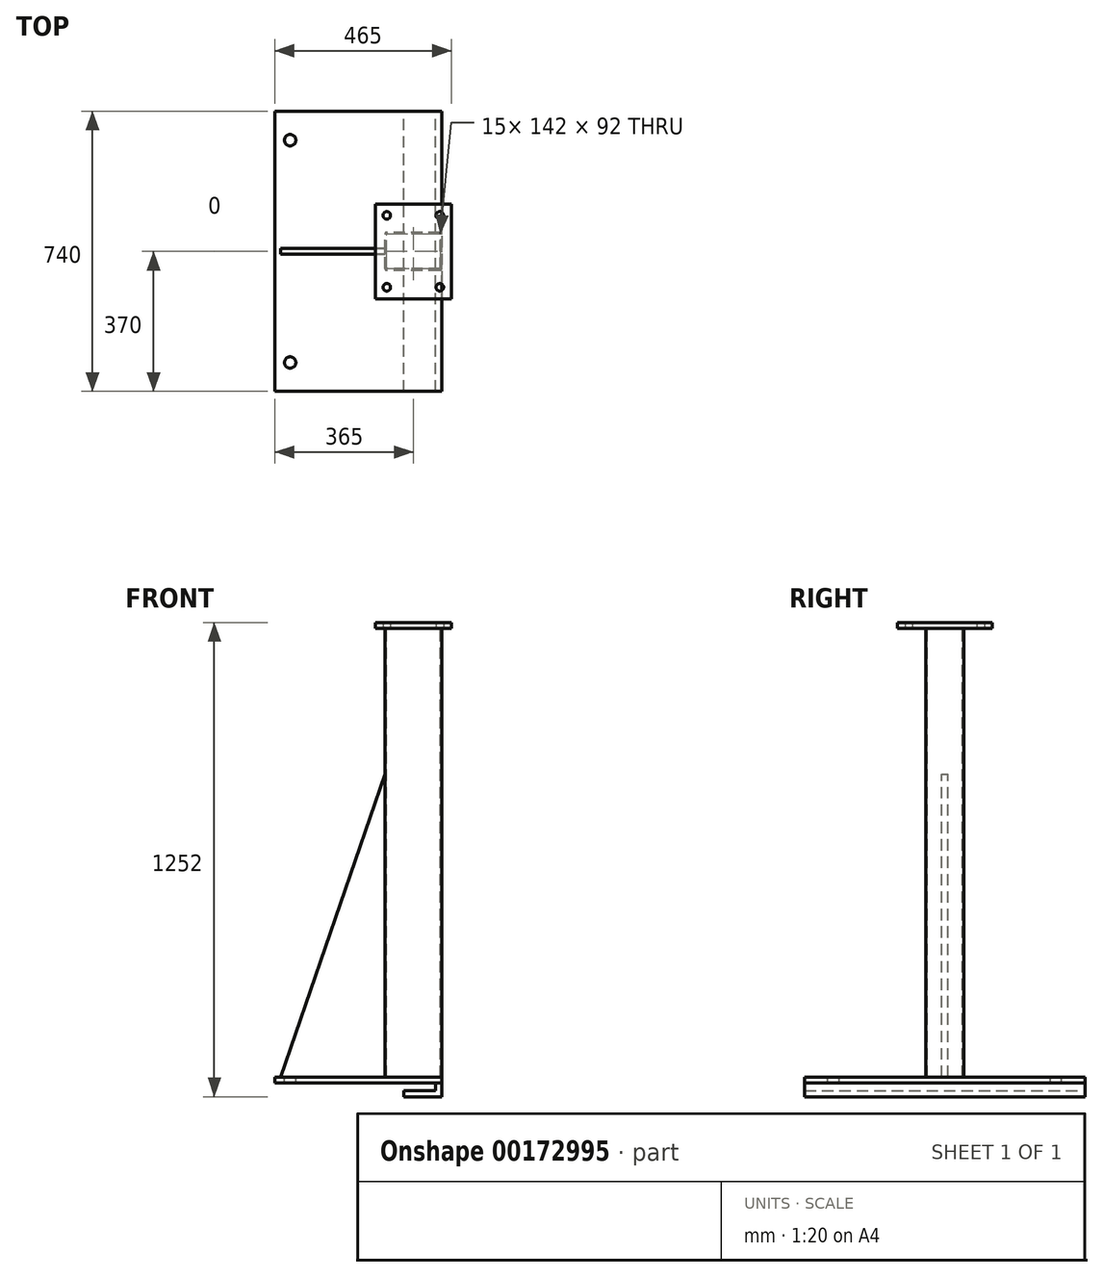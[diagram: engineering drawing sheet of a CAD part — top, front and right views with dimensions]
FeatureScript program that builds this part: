
annotation { "Feature Type Name" : "Feature", "Feature Type Description" : "" }
export const myFeature = defineFeature(function(context is Context, id is Id, definition is map)
    precondition{}
    {
        {
            var Q0;
            Q0=qCreatedBy(makeId("Top.planeOp"),FACE);
            var sketch = newSketch(context, id + "F0", { "sketchPlane" : qUnion([Q0])});
            skLineSegment(sketch, "E0.bottom", {"start": v(0, 0) * mm, "end": v(-150, 0) * mm});
            skLineSegment(sketch, "E0.top", {"start": v(0, 100) * mm, "end": v(-150, 100) * mm});
            skLineSegment(sketch, "E0.left", {"start": v(0, 0) * mm, "end": v(0, 100) * mm});
            skLineSegment(sketch, "E0.right", {"start": v(-150, 0) * mm, "end": v(-150, 100) * mm});
            skLineSegment(sketch, "E1.0", {"start": v(-4, 96) * mm, "end": v(-146, 96) * mm});
            skLineSegment(sketch, "E1.1", {"start": v(-4, 4) * mm, "end": v(-4, 96) * mm});
            skLineSegment(sketch, "E1.2", {"start": v(-4, 4) * mm, "end": v(-146, 4) * mm});
            skLineSegment(sketch, "E1.3", {"start": v(-146, 4) * mm, "end": v(-146, 96) * mm});
            skSolve(sketch);
        }
        {
            var Q0;
            Q0=makeQuery(id+"F0.imprint","IMPRINT",FACE,{"disambiguationData":[TD([[makeQuery(id+"F0.imprint","IMPRINT",EDGE,{"derivedFrom":sQuery(id+"F0.wireOp",EDGE,"E0.bottom")}),-1.0]])]});
            extrude(context, id + "F1", {"entities" : qUnion([Q0]), "oppositeDirection" : true, "depth" : 1184 * mm});
        }
        {
            var Q0;
            Q0=makeQuery(id+"F1.opExtrude","CAP_FACE",FACE,{"disambiguationData":[OSD([sQuery(id+"F0.wireOp",EDGE,"E0.bottom"),sQuery(id+"F0.wireOp",EDGE,"E0.top"),sQuery(id+"F0.wireOp",EDGE,"E0.left"),sQuery(id+"F0.wireOp",EDGE,"E0.right"),sQuery(id+"F0.wireOp",EDGE,"E1.0"),sQuery(id+"F0.wireOp",EDGE,"E1.1"),sQuery(id+"F0.wireOp",EDGE,"E1.2"),sQuery(id+"F0.wireOp",EDGE,"E1.3")])],"isStart":false});
            var sketch = newSketch(context, id + "F2", { "sketchPlane" : qUnion([Q0])});
            skLineSegment(sketch, "E2", {"start": v(0, 0) * mm, "end": v(0, 320) * mm});
            skLineSegment(sketch, "E3", {"start": v(0, -100) * mm, "end": v(0, -420) * mm});
            skLineSegment(sketch, "E4", {"start": v(0, 320) * mm, "end": v(-440, 320) * mm});
            skLineSegment(sketch, "E5", {"start": v(-440, 320) * mm, "end": v(-440, -420) * mm});
            skLineSegment(sketch, "E6", {"start": v(-440, -420) * mm, "end": v(0, -420) * mm});
            skCircle(sketch, "E7", {"center": v(-400, 243.5) * mm, "radius": 15 * mm});
            skLineSegment(sketch, "E8", {"start": v(-440, -50) * mm, "end": v(0, -50) * mm, "construction": true});
            skCircle(sketch, "E9.MirrorC", {"center": v(-400, -343.5) * mm, "radius": 15 * mm});
            skLineSegment(sketch, "E10", {"start": v(0, 0) * mm, "end": v(0, -100) * mm});
            skSolve(sketch);
        }
        {
            var Q0;
            Q0=makeQuery(id+"F2.imprint","IMPRINT",FACE,{"disambiguationData":[TD([[makeQuery(id+"F2.imprint","IMPRINT",EDGE,{"derivedFrom":sQuery(id+"F2.wireOp",EDGE,"E2")}),1.0]])]});
            var Q1;
            Q1=makeQuery(id+"F2.imprint","IMPRINT",FACE,{"disambiguationData":[TD([[makeQuery(id+"F2.imprint","IMPRINT",EDGE,{"derivedFrom":sQuery(id+"F2.wireOp",EDGE,"E10")}),-1.0]])]});
            var Q2;
            Q2=makeQuery(id+"F2.imprint","IMPRINT",FACE,{"disambiguationData":[TD([[makeQuery(id+"F2.imprint","IMPRINT",EDGE,{"derivedFrom":makeQuery(id+"F1.opExtrude","CAP_EDGE",EDGE,{"disambiguationData":[OSD([sQuery(id+"F0.wireOp",EDGE,"E1.0")])],"isStart":false})}),-1.0]])]});
            extrude(context, id + "F3", {"entities" : qUnion([Q0, Q1, Q2]), "depth" : 16 * mm});
        }
        {
            var Q0;
            Q0=makeQuery(id+"F1.opExtrude","SWEPT_FACE",FACE,{"disambiguationData":[OSD([sQuery(id+"F0.wireOp",EDGE,"E0.bottom")])]});
            cPlane(context, id + "F4", {"entities" : qUnion([Q0]), "cplaneType" : CPlaneType.OFFSET, "offset" : 50 * mm, "oppositeDirection" : true, "width" : 150 * mm, "height" : 150 * mm});
        }
        {
            var Q0;
            Q0=qCreatedBy(id+"F4.planeOp",FACE);
            var sketch = newSketch(context, id + "F5", { "sketchPlane" : qUnion([Q0])});
            skLineSegment(sketch, "E11.0", {"start": v(0, -1184) * mm, "end": v(-440, -1184) * mm});
            skLineSegment(sketch, "E11.1", {"start": v(-150, -1184) * mm, "end": v(-150, 0) * mm});
            skLineSegment(sketch, "E12", {"start": v(-425, -1184) * mm, "end": v(-150, -384) * mm});
            skSolve(sketch);
        }
        {
            var Q0;
            Q0 = qSketchRegion(id + "F5", true);
            extrude(context, id + "F6", {"entities" : qUnion([Q0]), "endBound" : BoundingType.SYMMETRIC, "depth" : 16 * mm});
        }
        {
            var Q0;
            Q0=qCreatedBy(id+"F4.planeOp",FACE);
            var sketch = newSketch(context, id + "F7", { "sketchPlane" : qUnion([Q0])});
            skLineSegment(sketch, "E13.0", {"start": v(0, -1200) * mm, "end": v(-440, -1200) * mm});
            skLineSegment(sketch, "E13.1", {"start": v(0, -1200) * mm, "end": v(0, -1184) * mm});
            skLineSegment(sketch, "E14", {"start": v(0, -1200) * mm, "end": v(0, -1236) * mm});
            skLineSegment(sketch, "E15", {"start": v(0, -1236) * mm, "end": v(-100, -1236) * mm});
            skLineSegment(sketch, "E16", {"start": v(-100, -1236) * mm, "end": v(-100, -1220) * mm});
            skLineSegment(sketch, "E17", {"start": v(-100, -1220) * mm, "end": v(-16, -1220) * mm});
            skLineSegment(sketch, "E18", {"start": v(-16, -1220) * mm, "end": v(-16, -1200) * mm});
            skSolve(sketch);
        }
        {
            var Q0;
            {var subQ0=sQuery(id+"F7.wireOp",EDGE,"E14");Q0=makeQuery(id+"F7.imprint","IMPRINT",FACE,{"disambiguationData":[TD([[makeQuery(id+"F7.imprint","IMPRINT",EDGE,{"derivedFrom":subQ0}),-1.0]])]});}
            extrude(context, id + "F8", {"entities" : qUnion([Q0]), "endBound" : BoundingType.SYMMETRIC, "depth" : 740 * mm});
        }
        {
            var Q0;
            Q0=makeQuery(id+"F1.opExtrude","CAP_FACE",FACE,{"disambiguationData":[OSD([sQuery(id+"F0.wireOp",EDGE,"E0.bottom"),sQuery(id+"F0.wireOp",EDGE,"E0.top"),sQuery(id+"F0.wireOp",EDGE,"E0.left"),sQuery(id+"F0.wireOp",EDGE,"E0.right"),sQuery(id+"F0.wireOp",EDGE,"E1.0"),sQuery(id+"F0.wireOp",EDGE,"E1.1"),sQuery(id+"F0.wireOp",EDGE,"E1.2"),sQuery(id+"F0.wireOp",EDGE,"E1.3")])],"isStart":true});
            var sketch = newSketch(context, id + "F9", { "sketchPlane" : qUnion([Q0])});
            skLineSegment(sketch, "E19.bottom", {"start": v(-175, 175) * mm, "end": v(25, 175) * mm});
            skLineSegment(sketch, "E19.top", {"start": v(-175, -75) * mm, "end": v(25, -75) * mm});
            skLineSegment(sketch, "E19.left", {"start": v(-175, 175) * mm, "end": v(-175, -75) * mm});
            skLineSegment(sketch, "E19.right", {"start": v(25, 175) * mm, "end": v(25, -75) * mm});
            skCircle(sketch, "E20", {"center": v(-145, 145) * mm, "radius": 10 * mm});
            skLineSegment(sketch, "E21", {"start": v(-75, 175) * mm, "end": v(-75, -75) * mm, "construction": true});
            skLineSegment(sketch, "E22", {"start": v(-175, 50) * mm, "end": v(25, 50) * mm, "construction": true});
            skCircle(sketch, "E23.MirrorC", {"center": v(-5, 145) * mm, "radius": 10 * mm});
            skCircle(sketch, "E24.MirrorC", {"center": v(-145, -45) * mm, "radius": 10 * mm});
            skCircle(sketch, "E25.MirrorC", {"center": v(-5, -45) * mm, "radius": 10 * mm});
            skSolve(sketch);
        }
        {
            var Q0;
            Q0=makeQuery(id+"F9.imprint","IMPRINT",FACE,{"disambiguationData":[TD([[makeQuery(id+"F9.imprint","IMPRINT",EDGE,{"derivedFrom":makeQuery(id+"F1.opExtrude","CAP_EDGE",EDGE,{"disambiguationData":[OSD([sQuery(id+"F0.wireOp",EDGE,"E0.bottom")])],"isStart":true})}),-1.0]])]});
            var Q1;
            Q1=makeQuery(id+"F9.imprint","IMPRINT",FACE,{"disambiguationData":[TD([[makeQuery(id+"F9.imprint","IMPRINT",EDGE,{"derivedFrom":makeQuery(id+"F1.opExtrude","CAP_EDGE",EDGE,{"disambiguationData":[OSD([sQuery(id+"F0.wireOp",EDGE,"E1.0")])],"isStart":true})}),1.0]])]});
            var Q2;
            Q2=makeQuery(id+"F9.imprint","IMPRINT",FACE,{"disambiguationData":[TD([[makeQuery(id+"F9.imprint","IMPRINT",EDGE,{"derivedFrom":sQuery(id+"F9.wireOp",EDGE,"E19.bottom")}),-1.0]])]});
            extrude(context, id + "F10", {"entities" : qUnion([Q0, Q1, Q2]), "depth" : 16 * mm});
        }
        {
            var Q0;
            Q0=makeQuery(id+"F1.opExtrude","SWEPT_EDGE",EDGE,{"disambiguationData":[OSD([sQuery(id+"F0.wireOp",EDGE,"E0.bottom"),sQuery(id+"F0.wireOp",EDGE,"E0.left")])]});
            var Q1;
            Q1=makeQuery(id+"F1.opExtrude","SWEPT_EDGE",EDGE,{"disambiguationData":[OSD([sQuery(id+"F0.wireOp",EDGE,"E0.bottom"),sQuery(id+"F0.wireOp",EDGE,"E0.right")])]});
            var Q2;
            Q2=makeQuery(id+"F1.opExtrude","SWEPT_EDGE",EDGE,{"disambiguationData":[OSD([sQuery(id+"F0.wireOp",EDGE,"E0.top"),sQuery(id+"F0.wireOp",EDGE,"E0.right")])]});
            var Q3;
            Q3=makeQuery(id+"F1.opExtrude","SWEPT_EDGE",EDGE,{"disambiguationData":[OSD([sQuery(id+"F0.wireOp",EDGE,"E0.top"),sQuery(id+"F0.wireOp",EDGE,"E0.left")])]});
            fillet(context, id + "F11", {"entities" : qUnion([Q0, Q1, Q2, Q3]), "radius" : 5 * mm, "tangentPropagation" : true, "allowEdgeOverflow" : false});
        }
    });
